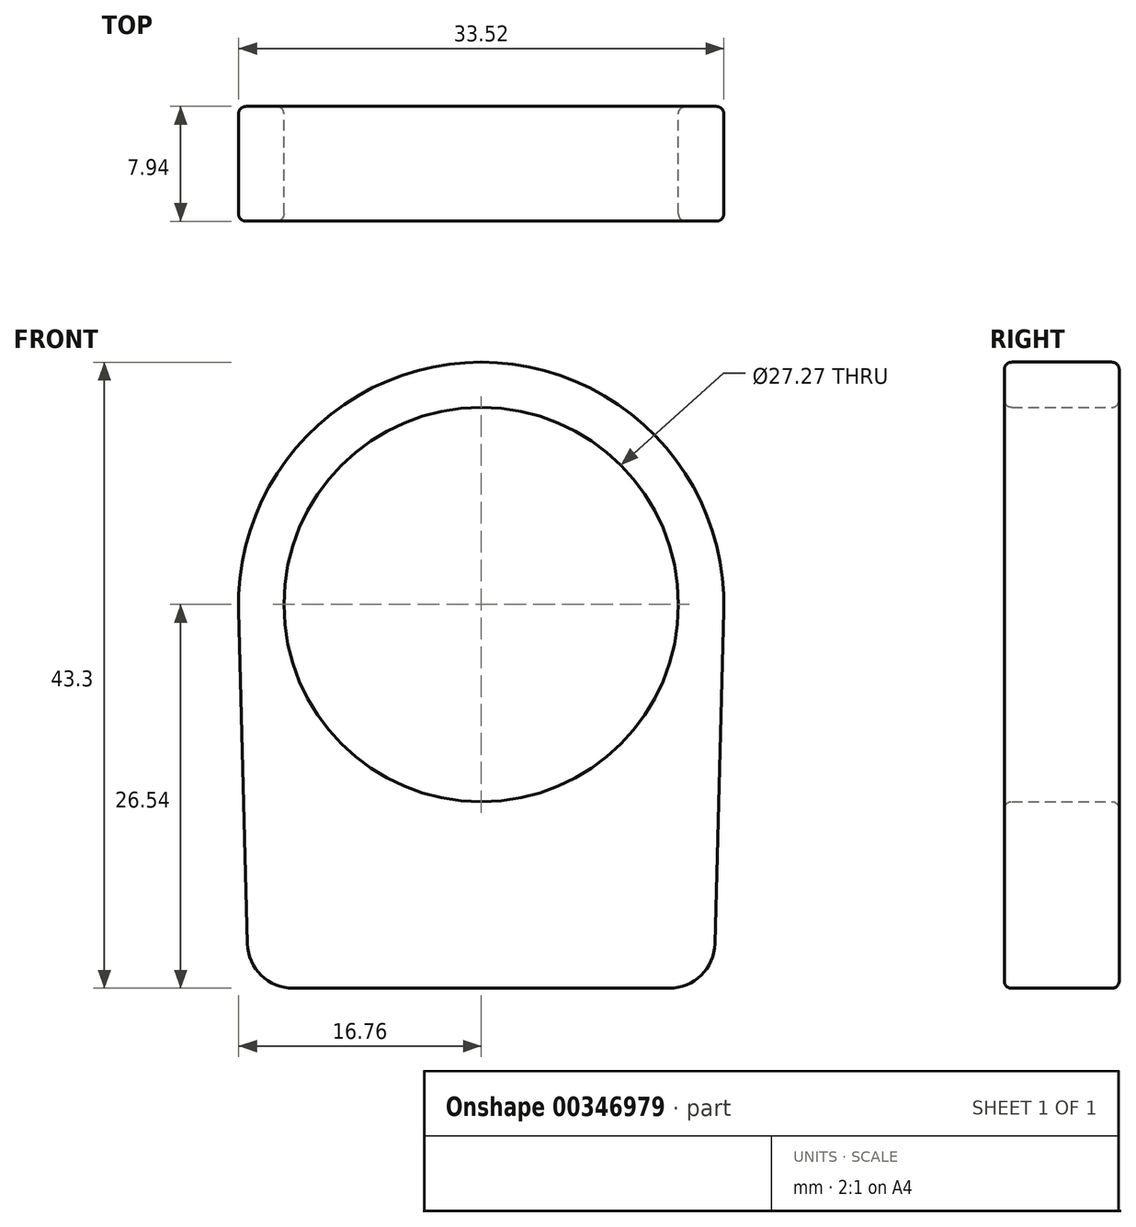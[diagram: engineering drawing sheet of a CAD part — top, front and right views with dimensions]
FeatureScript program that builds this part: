
annotation { "Feature Type Name" : "Feature", "Feature Type Description" : "" }
export const myFeature = defineFeature(function(context is Context, id is Id, definition is map)
    precondition{}
    {
        {
            var Q0;
            Q0=qCreatedBy(makeId("Front.planeOp"),FACE);
            var sketch = newSketch(context, id + "F0", { "sketchPlane" : qUnion([Q0])});
            skCircle(sketch, "E0", {"center": v(0, 0) * mm, "radius": 13.63 * mm});
            skArc(sketch, "E1", {"start": v(16.76, -0.44) * mm, "mid": v(0, 16.76) * mm, "end": v(-16.76, -0.44) * mm});
            skLineSegment(sketch, "E2", {"start": v(-12.98, -26.54) * mm, "end": v(12.98, -26.54) * mm});
            skLineSegment(sketch, "E3", {"start": v(-16.16, -23.45) * mm, "end": v(-16.76, -0.44) * mm});
            skLineSegment(sketch, "E4", {"start": v(16.16, -23.45) * mm, "end": v(16.76, -0.44) * mm});
            skPoint(sketch, "E5", {"position": v(0, -26.54) * mm});
            skPoint(sketch, "E6.visualSharp", {"position": v(-16.07, -26.54) * mm});
            skArc(sketch, "E6.filletArc", {"start": v(-16.16, -23.45) * mm, "mid": v(-15.2, -25.64) * mm, "end": v(-12.98, -26.54) * mm});
            skPoint(sketch, "E7.visualSharp", {"position": v(16.07, -26.54) * mm});
            skArc(sketch, "E7.filletArc", {"start": v(12.98, -26.54) * mm, "mid": v(15.2, -25.64) * mm, "end": v(16.16, -23.45) * mm});
            skSolve(sketch);
        }
        {
            var Q0;
            Q0 = qSketchRegion(id + "F0", true);
            extrude(context, id + "F1", {"entities" : qUnion([Q0]), "depth" : 7.94 * mm, "symmetric" : true});
        }
        {
            var Q0;
            Q0=makeQuery(id+"F1.opExtrude","CAP_FACE",FACE,{"disambiguationData":[OSD([sQuery(id+"F0.wireOp",EDGE,"E0"),sQuery(id+"F0.wireOp",EDGE,"E1"),sQuery(id+"F0.wireOp",EDGE,"E2"),sQuery(id+"F0.wireOp",EDGE,"E3"),sQuery(id+"F0.wireOp",EDGE,"E4"),sQuery(id+"F0.wireOp",EDGE,"E6.filletArc"),sQuery(id+"F0.wireOp",EDGE,"E7.filletArc")])],"isStart":false});
            var Q1;
            Q1=makeQuery(id+"F1.opExtrude","CAP_FACE",FACE,{"disambiguationData":[OSD([sQuery(id+"F0.wireOp",EDGE,"E0"),sQuery(id+"F0.wireOp",EDGE,"E1"),sQuery(id+"F0.wireOp",EDGE,"E2"),sQuery(id+"F0.wireOp",EDGE,"E3"),sQuery(id+"F0.wireOp",EDGE,"E4"),sQuery(id+"F0.wireOp",EDGE,"E6.filletArc"),sQuery(id+"F0.wireOp",EDGE,"E7.filletArc")])],"isStart":true});
            fillet(context, id + "F2", {"entities" : qUnion([Q0, Q1]), "radius" : 0.5 * mm, "tangentPropagation" : true, "allowEdgeOverflow" : false});
        }
    });
